# Revit family: Casement_38_A_Top_Hung_Standard
name_source: partatom
category: Windows
revit_build: Autodesk Revit 2014 (Build: 20130308_1515(x64)
units: mm (PartAtom-declared; Revit-internal decimal feet)

## types (6) — shared parameters
Aluminium Thickness = 1 mm  [stored 0.00328084 ft]
Bead SG Gap = 13 mm  [stored 0.0426509 ft]
Bottom Hung = No
Casement Dimension = 38 mm  [stored 0.124672 ft]
Custom Window Height = 590 mm  [stored 1.9357 ft]
DG Extrusion Start = 9 mm  [stored 0.0295276 ft]
DG Gasket Finish = Double Glazing Gasket Material
DG Thickness Calc = 4 mm  [stored 0.0131234 ft]
Default Sill Height = 800 mm  [stored 2.62467 ft]
Depth Bead = 24 mm  [stored 0.0787402 ft]
Description = Window 38mm, Type A top hung
Frame Center Offset = 19 mm  [stored 0.062336 ft]
Height = 590 mm  [stored 1.9357 ft]
Height Sash = 514 mm  [stored 1.68635 ft]
Height Sash 1 Opening = 545 mm  [stored 1.78806 ft]
Limit Sash Height Max = 1200 mm
Limit Sash Height Min = 300 mm  [stored 0.984252 ft]
Limit Sash Width Max = 1500 mm  [stored 4.92126 ft]
Limit Sash Width Min = 300 mm  [stored 0.984252 ft]
Limit Window Height Max = 1246 mm  [stored 4.08793 ft]
Limit Window Height Min = 346 mm
Limit Window Width Max = 1546 mm  [stored 5.07218 ft]
Limit Window Width Min = 346 mm
Manufacturer = Crealco
Max System DG One Piece Thickness = 6 mm  [stored 0.019685 ft]
Max System DG Unit Thickness = 25 mm  [stored 0.082021 ft]
Model = Casement 38
Offset Bead SG Center Reversed = 19 mm  [stored 0.062336 ft]
Offset Sash 1 Top = 23 mm  [stored 0.0754593 ft]
Offset Sash Left = 23 mm  [stored 0.0754593 ft]
Offset Window Exterior = 19 mm  [stored 0.062336 ft]
SG Gasket Thickness = 6 mm  [stored 0.019685 ft]
Sash Center Offset = 16 mm  [stored 0.0524934 ft]
Sash Height = 545 mm  [stored 1.78806 ft]
Sash Overlap = 7 mm  [stored 0.0229659 ft]
Sash Spacing Inner = 8 mm  [stored 0.0262467 ft]
Top Hung = Yes
URL = http://www.crealco.co.za
Wall Closure = By host
Width Bead = 15 mm  [stored 0.0492126 ft]
Width Profile = 30 mm  [stored 0.0984252 ft]
zero-valued in all types: Window Exterior Offset

## per-type parameters (varying)
| type | Clearvue Insulated LowE SHGC Value | Clearvue Insulated LowE U Value | Clearvue Insulated SHGC Value | Clearvue Insulated U Value | Clearvue SHGC Value | Clearvue U Value | Custom Windload | Custom Window Width | Energy Advantage SHGC Value | Energy Advantage U Value | Intruderprufe Insulated LowE SHGC Value | Intruderprufe Insulated LowE U Value | Intruderprufe Insulated SHGC Value | Intruderprufe Insulated U Value | Intruderprufe LowE SHGC Value | Intruderprufe LowE U Value | Intruderprufe SHGC Value | Intruderprufe U Value | Max Pane Area | Sash Width | Width | Width Sash | Width Sash Opening | Windload Design |
| 38-0606T-1000Pa | 0.41 | 4.07 | 0.45 | 4.48 | 0.514 | 6.21 | 1000 mm  [stored 3.28084 ft] | 590 mm  [stored 1.9357 ft] | 0.461 | 5.03 | 0.384 | 3.97 | 0.421 | 4.38 | 0.436 | 4.92 | 0.487 | 6.12 | 0.2 m² | 545 mm  [stored 1.78806 ft] | 590 mm  [stored 1.9357 ft] | 514 mm  [stored 1.68635 ft] | 545 mm  [stored 1.78806 ft] | 1000 mm  [stored 3.28084 ft] |
| 38-0606T-1500Pa | 0.41 | 4.07 | 0.45 | 4.48 | 0.514 | 6.21 | 1500 mm  [stored 4.92126 ft] | 590 mm  [stored 1.9357 ft] | 0.461 | 5.03 | 0.384 | 3.97 | 0.421 | 4.38 | 0.436 | 4.92 | 0.487 | 6.12 | 0.2 m² | 545 mm  [stored 1.78806 ft] | 590 mm  [stored 1.9357 ft] | 514 mm  [stored 1.68635 ft] | 545 mm  [stored 1.78806 ft] | 1500 mm  [stored 4.92126 ft] |
| 38-0606T-2000Pa | 0.41 | 4.07 | 0.45 | 4.48 | 0.514 | 6.21 | 2000 mm  [stored 6.56168 ft] | 590 mm  [stored 1.9357 ft] | 0.461 | 5.03 | 0.384 | 3.97 | 0.421 | 4.38 | 0.436 | 4.92 | 0.487 | 6.12 | 0.2 m² | 545 mm  [stored 1.78806 ft] | 590 mm  [stored 1.9357 ft] | 514 mm  [stored 1.68635 ft] | 545 mm  [stored 1.78806 ft] | 2000 mm  [stored 6.56168 ft] |
| 38-0906T-1000Pa | 0.449 | 3.77 | 0.493 | 4.24 | 0.563 | 6.16 | 1000 mm  [stored 3.28084 ft] | 890 mm  [stored 2.91995 ft] | 0.505 | 4.83 | 0.419 | 3.67 | 0.46 | 4.13 | 0.476 | 4.73 | 0.533 | 6.07 | 0.33 m² | 845 mm  [stored 2.77231 ft] | 890 mm  [stored 2.91995 ft] | 814 mm  [stored 2.6706 ft] | 845 mm  [stored 2.77231 ft] | 1000 mm  [stored 3.28084 ft] |
| 38-0906T-1500Pa | 0.449 | 3.77 | 0.493 | 4.24 | 0.563 | 6.16 | 1500 mm  [stored 4.92126 ft] | 890 mm  [stored 2.91995 ft] | 0.505 | 4.83 | 0.419 | 3.67 | 0.46 | 4.13 | 0.476 | 4.73 | 0.533 | 6.07 | 0.33 m² | 845 mm  [stored 2.77231 ft] | 890 mm  [stored 2.91995 ft] | 814 mm  [stored 2.6706 ft] | 845 mm  [stored 2.77231 ft] | 1500 mm  [stored 4.92126 ft] |
| 38-0906T-2000Pa | 0.449 | 3.77 | 0.493 | 4.24 | 0.563 | 6.16 | 2000 mm  [stored 6.56168 ft] | 890 mm  [stored 2.91995 ft] | 0.505 | 4.83 | 0.419 | 3.67 | 0.46 | 4.13 | 0.476 | 4.73 | 0.533 | 6.07 | 0.33 m² | 845 mm  [stored 2.77231 ft] | 890 mm  [stored 2.91995 ft] | 814 mm  [stored 2.6706 ft] | 845 mm  [stored 2.77231 ft] | 2000 mm  [stored 6.56168 ft] |

note: [stored X ft] marks values corroborated as IEEE doubles in the binary element streams (Revit-internal decimal feet)

## geometry (parser evidence)
native form markers: Extrusion x1, Sweep x28
no freeform markers — native parametric forms only
